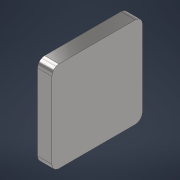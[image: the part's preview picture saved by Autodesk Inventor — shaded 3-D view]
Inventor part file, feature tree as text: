
AUTODESK INVENTOR PART (.ipt)
format: ipt  version: 2022 (Build 260153000, 153)  size: 96,768 bytes
history: native  units: mm
features: extrude x1, fillet x1, sketch x1
ambient origin geometry x8: Origin, YZ Plane, XZ Plane, XY Plane, X Axis, Y Axis, Z Axis, Center Point
bodies: Solid1 (feature_tree)
feature tree (3):
  extrude  "Extrusion1"  Depth=25.2mm
  fillet  "Fillet1"  Radius=4.0mm
  sketch  "Sketch1"  dims[d0=25.2mm d1=25.2mm d2=4.0mm d3=0.0mm d4=2.0mm]
